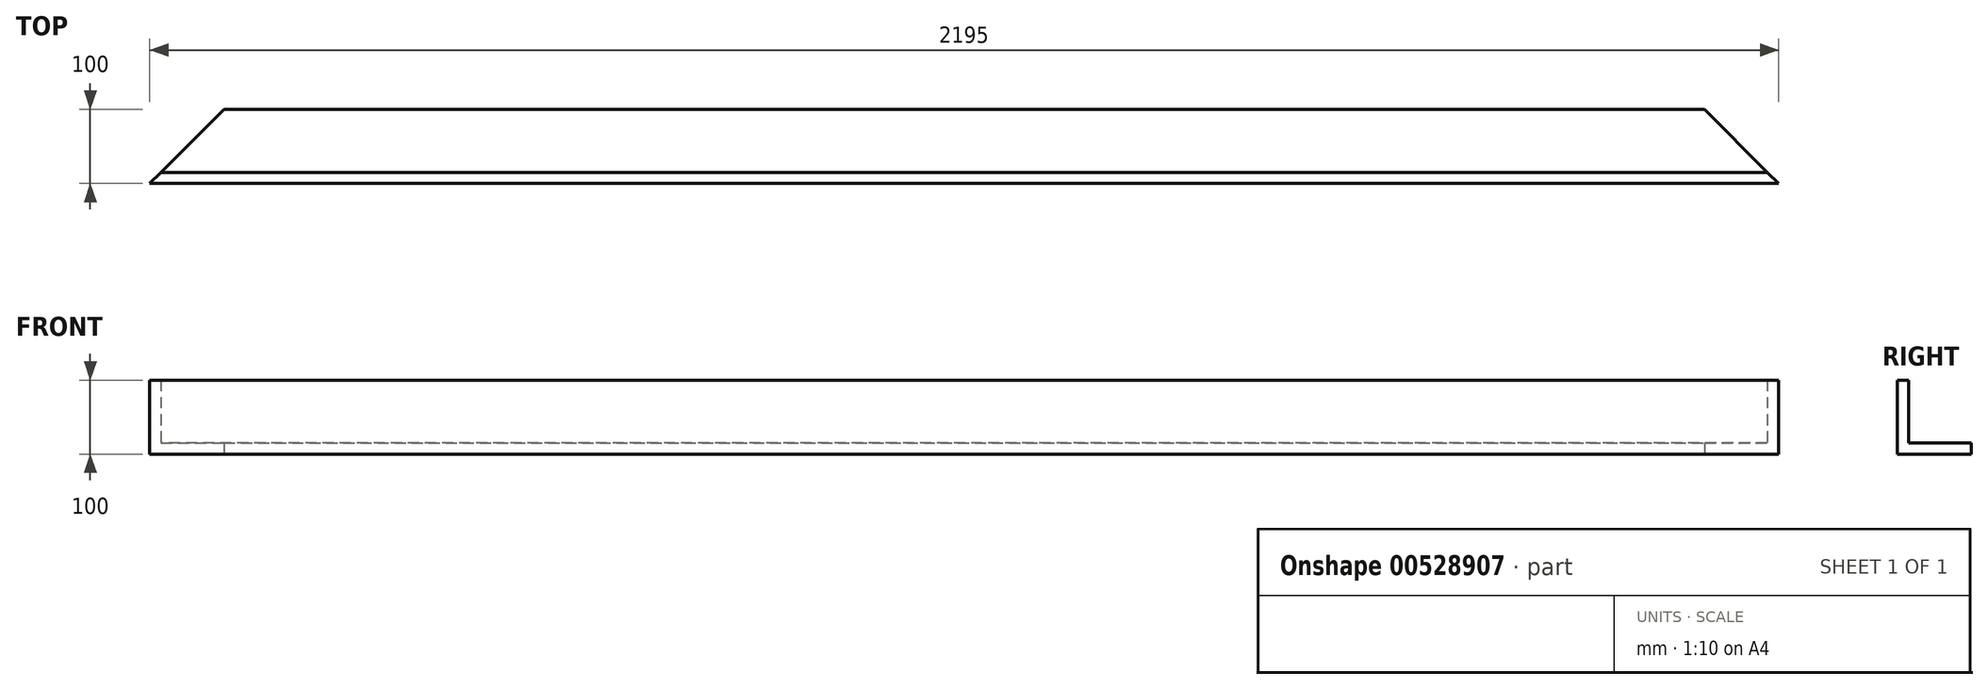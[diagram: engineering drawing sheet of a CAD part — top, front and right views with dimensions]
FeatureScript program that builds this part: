
annotation { "Feature Type Name" : "Feature", "Feature Type Description" : "" }
export const myFeature = defineFeature(function(context is Context, id is Id, definition is map)
    precondition{}
    {
        {
            var Q0;
            Q0=qCreatedBy(makeId("Top.planeOp"),FACE);
            var sketch = newSketch(context, id + "F0", { "sketchPlane" : qUnion([Q0])});
            skLineSegment(sketch, "E0", {"start": v(28.05, 0) * mm, "end": v(-28.05, 0) * mm, "construction": true});
            skLineSegment(sketch, "E1", {"start": v(1097.5, 100) * mm, "end": v(-1097.5, 100) * mm});
            skLineSegment(sketch, "E2", {"start": v(-1097.5, 100) * mm, "end": v(-997.5, 200) * mm});
            skLineSegment(sketch, "E3", {"start": v(-997.5, 200) * mm, "end": v(997.5, 200) * mm});
            skLineSegment(sketch, "E4", {"start": v(997.5, 200) * mm, "end": v(1097.5, 100) * mm});
            skLineSegment(sketch, "E5", {"start": v(0, 0) * mm, "end": v(0, 100) * mm, "construction": true});
            skSolve(sketch);
        }
        {
            var Q0;
            Q0 = qSketchRegion(id + "F0", true);
            extrude(context, id + "F1", {"entities" : qUnion([Q0]), "depth" : 15 * mm, "offsetDistance" : 25 * mm});
        }
        {
            var Q0;
            Q0=makeQuery(id+"F1.opExtrude","CAP_FACE",FACE,{"disambiguationData":[OSD([sQuery(id+"F0.wireOp",EDGE,"E1"),sQuery(id+"F0.wireOp",EDGE,"E2"),sQuery(id+"F0.wireOp",EDGE,"E3"),sQuery(id+"F0.wireOp",EDGE,"E4")])],"isStart":false});
            var sketch = newSketch(context, id + "F2", { "sketchPlane" : qUnion([Q0])});
            skLineSegment(sketch, "E6.0", {"start": v(1097.5, 100) * mm, "end": v(-1097.5, 100) * mm});
            skLineSegment(sketch, "E7", {"start": v(1082.5, 115) * mm, "end": v(-1082.5, 115) * mm});
            skLineSegment(sketch, "E8", {"start": v(-1082.5, 115) * mm, "end": v(-1097.5, 100) * mm});
            skLineSegment(sketch, "E9", {"start": v(1097.5, 100) * mm, "end": v(1082.5, 115) * mm});
            skSolve(sketch);
        }
        {
            var Q0;
            Q0=makeQuery(id+"F2.imprint","IMPRINT",FACE,{"disambiguationData":[TD([[makeQuery(id+"F2.imprint","IMPRINT",EDGE,{"derivedFrom":sQuery(id+"F2.wireOp",EDGE,"E6.0")}),-1.0]])]});
            extrude(context, id + "F3", {"entities" : qUnion([Q0]), "operationType" : NewBodyOperationType.ADD, "depth" : (100 - 15) * mm, "offsetDistance" : 25 * mm});
        }
    });
